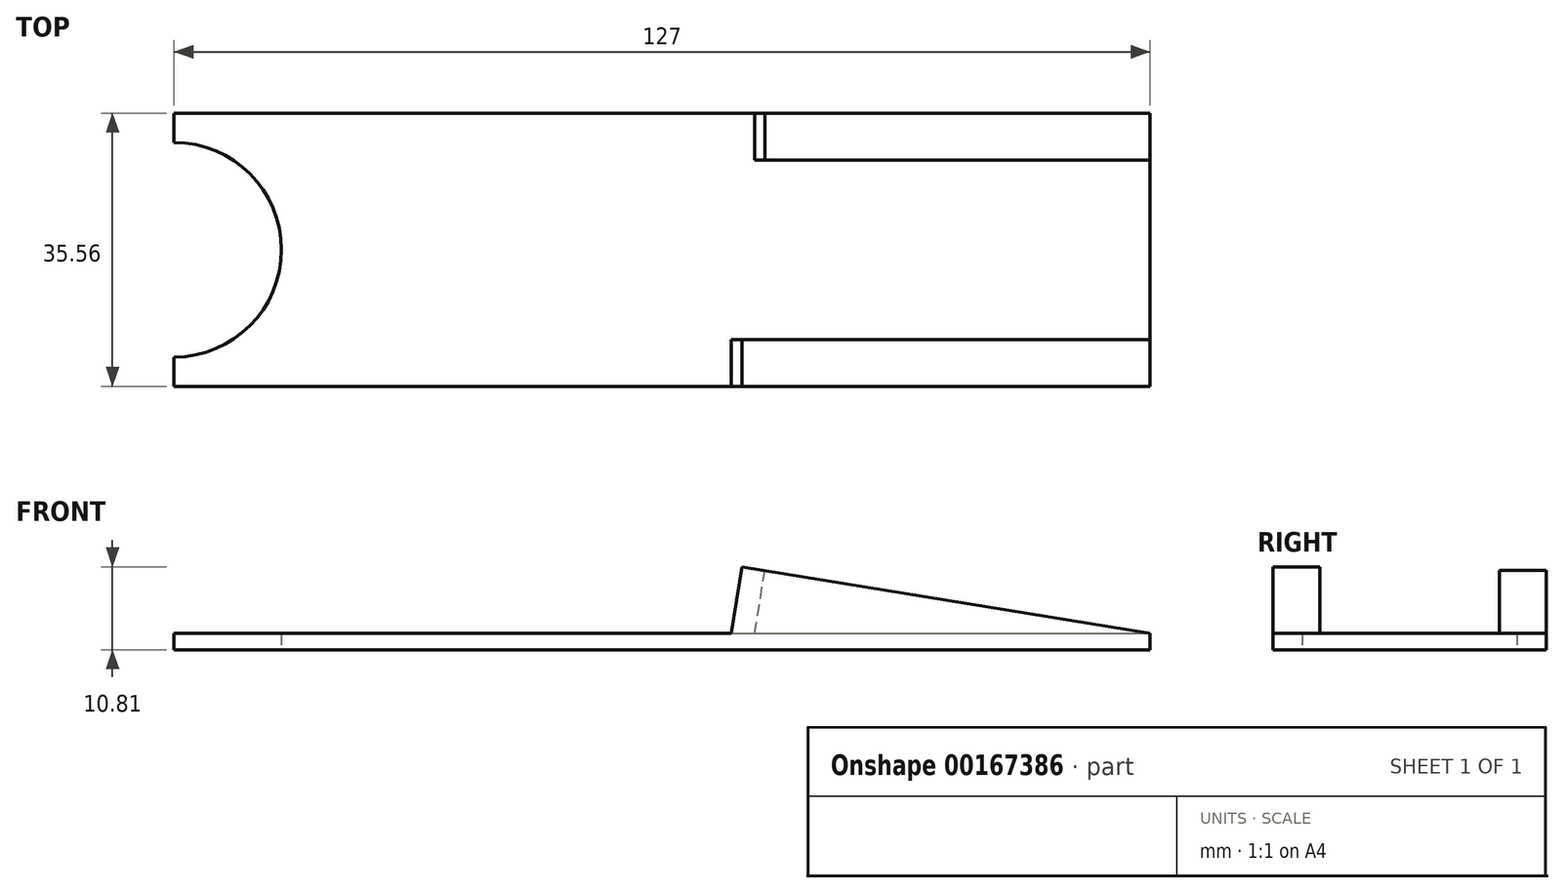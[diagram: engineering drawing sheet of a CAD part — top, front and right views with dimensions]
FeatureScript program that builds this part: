
annotation { "Feature Type Name" : "Feature", "Feature Type Description" : "" }
export const myFeature = defineFeature(function(context is Context, id is Id, definition is map)
    precondition{}
    {
        {
            var Q0;
            Q0=qCreatedBy(makeId("Top.planeOp"),FACE);
            var sketch = newSketch(context, id + "F0", { "sketchPlane" : qUnion([Q0])});
            skLineSegment(sketch, "E0.bottom", {"start": v(-27.13, -6.82) * mm, "end": v(99.87, -6.82) * mm});
            skLineSegment(sketch, "E0.top", {"start": v(-27.13, 28.74) * mm, "end": v(99.87, 28.74) * mm});
            skLineSegment(sketch, "E0.left", {"start": v(-27.13, -6.82) * mm, "end": v(-27.13, 28.74) * mm});
            skLineSegment(sketch, "E0.right", {"start": v(99.87, -6.82) * mm, "end": v(99.87, 28.74) * mm});
            skArc(sketch, "E1", {"start": v(-27.13, -3.01) * mm, "mid": v(-13.16, 10.96) * mm, "end": v(-27.13, 24.93) * mm});
            skSolve(sketch);
        }
        {
            var Q0;
            {var subQ3=sQuery(id+"F0.wireOp",EDGE,"E0.bottom");Q0=makeQuery(id+"F0.imprint","IMPRINT",FACE,{"disambiguationData":[TD([[makeQuery(id+"F0.imprint","IMPRINT",EDGE,{"derivedFrom":subQ3}),1.0]])]});}
            extrude(context, id + "F1", {"entities" : qUnion([Q0]), "depth" : 2.16 * mm});
        }
        {
            var Q0;
            {var subQ0=sQuery(id+"F0.wireOp",EDGE,"E0.left");Q0=makeQuery(id+"F1.opExtrude","SWEPT_FACE",FACE,{"disambiguationData":[OSD([subQ0]),TDD([makeQuery(id+"F0.imprint","IMPRINT",EDGE,{"disambiguationData":[TD([[makeQuery(id+"F0.imprint","INTERSECT",VERTEX,{"derivedFrom":[sQuery(id+"F0.wireOp",EDGE,"E0.top"),subQ0]}),1.0]])],"derivedFrom":subQ0})])]});}
            var sketch = newSketch(context, id + "F2", { "sketchPlane" : qUnion([Q0])});
            skLineSegment(sketch, "E2.0", {"start": v(6.82, 2.16) * mm, "end": v(6.82, 0) * mm});
            skLineSegment(sketch, "E3.bottom", {"start": v(6.82, 0) * mm, "end": v(-28.74, 0) * mm, "construction": true});
            skLineSegment(sketch, "E3.top", {"start": v(6.82, 22.86) * mm, "end": v(-28.74, 22.86) * mm, "construction": true});
            skLineSegment(sketch, "E3.left", {"start": v(6.82, 0) * mm, "end": v(6.82, 22.86) * mm, "construction": true});
            skLineSegment(sketch, "E3.right", {"start": v(-28.74, 0) * mm, "end": v(-28.74, 22.86) * mm, "construction": true});
            skSolve(sketch);
        }
        {
            var Q0;
            Q0=makeQuery(id+"F1.opExtrude","CAP_EDGE",EDGE,{"disambiguationData":[OSD([sQuery(id+"F0.wireOp",EDGE,"E0.right")])],"isStart":false});
            cPoint(context, id + "F3", {"entities" : qUnion([Q0]), "parameter" : 0.5});
        }
        {
            var Q0;
            Q0=sQuery(id+"F2.wireOp",VERTEX,"E3.top.start");
            var Q1;
            Q1=sQuery(id+"F2.wireOp",VERTEX,"E3.top.end");
            var Q2;
            Q2 = qCreatedBy(id + "F3" ,VERTEX);
            cPlane(context, id + "F4", {"entities" : qUnion([Q0, Q1, Q2]), "cplaneType" : CPlaneType.THREE_POINT, "offset" : 25.4 * mm, "width" : 152.4 * mm, "height" : 152.4 * mm});
        }
        {
            var Q0;
            Q0=qCreatedBy(id+"F4.planeOp",FACE);
            var sketch = newSketch(context, id + "F5", { "sketchPlane" : qUnion([Q0])});
            skLineSegment(sketch, "E4.0", {"start": v(98.22, -6.82) * mm, "end": v(98.22, 28.74) * mm});
            skLineSegment(sketch, "E5.bottom", {"start": v(98.22, -6.82) * mm, "end": v(44.44, -6.82) * mm});
            skLineSegment(sketch, "E5.top", {"start": v(98.22, -0.72) * mm, "end": v(44.44, -0.72) * mm});
            skLineSegment(sketch, "E5.left", {"start": v(98.22, -6.82) * mm, "end": v(98.22, -0.72) * mm});
            skLineSegment(sketch, "E5.right", {"start": v(44.44, -6.82) * mm, "end": v(44.44, -0.72) * mm});
            skLineSegment(sketch, "E6.bottom", {"start": v(98.22, 28.74) * mm, "end": v(47.44, 28.74) * mm});
            skLineSegment(sketch, "E6.top", {"start": v(98.22, 22.64) * mm, "end": v(47.44, 22.64) * mm});
            skLineSegment(sketch, "E6.left", {"start": v(98.22, 28.74) * mm, "end": v(98.22, 22.64) * mm});
            skLineSegment(sketch, "E6.right", {"start": v(47.44, 28.74) * mm, "end": v(47.44, 22.64) * mm});
            skSolve(sketch);
        }
        {
            var Q0;
            Q0 = qSketchRegion(id + "F5", true);
            var Q1;
            Q1=makeQuery(id+"F1.opExtrude","CAP_FACE",FACE,{"disambiguationData":[OSD([sQuery(id+"F0.wireOp",EDGE,"E0.bottom"),sQuery(id+"F0.wireOp",EDGE,"E0.top"),sQuery(id+"F0.wireOp",EDGE,"E0.left"),sQuery(id+"F0.wireOp",EDGE,"E0.right"),sQuery(id+"F0.wireOp",EDGE,"E1")])],"isStart":false});
            extrude(context, id + "F6", {"entities" : qUnion([Q0]), "operationType" : NewBodyOperationType.ADD, "endBound" : BoundingType.UP_TO_SURFACE, "oppositeDirection" : true, "endBoundEntityFace" : qUnion([Q1]), "depth" : 25.4 * mm});
        }
    });
